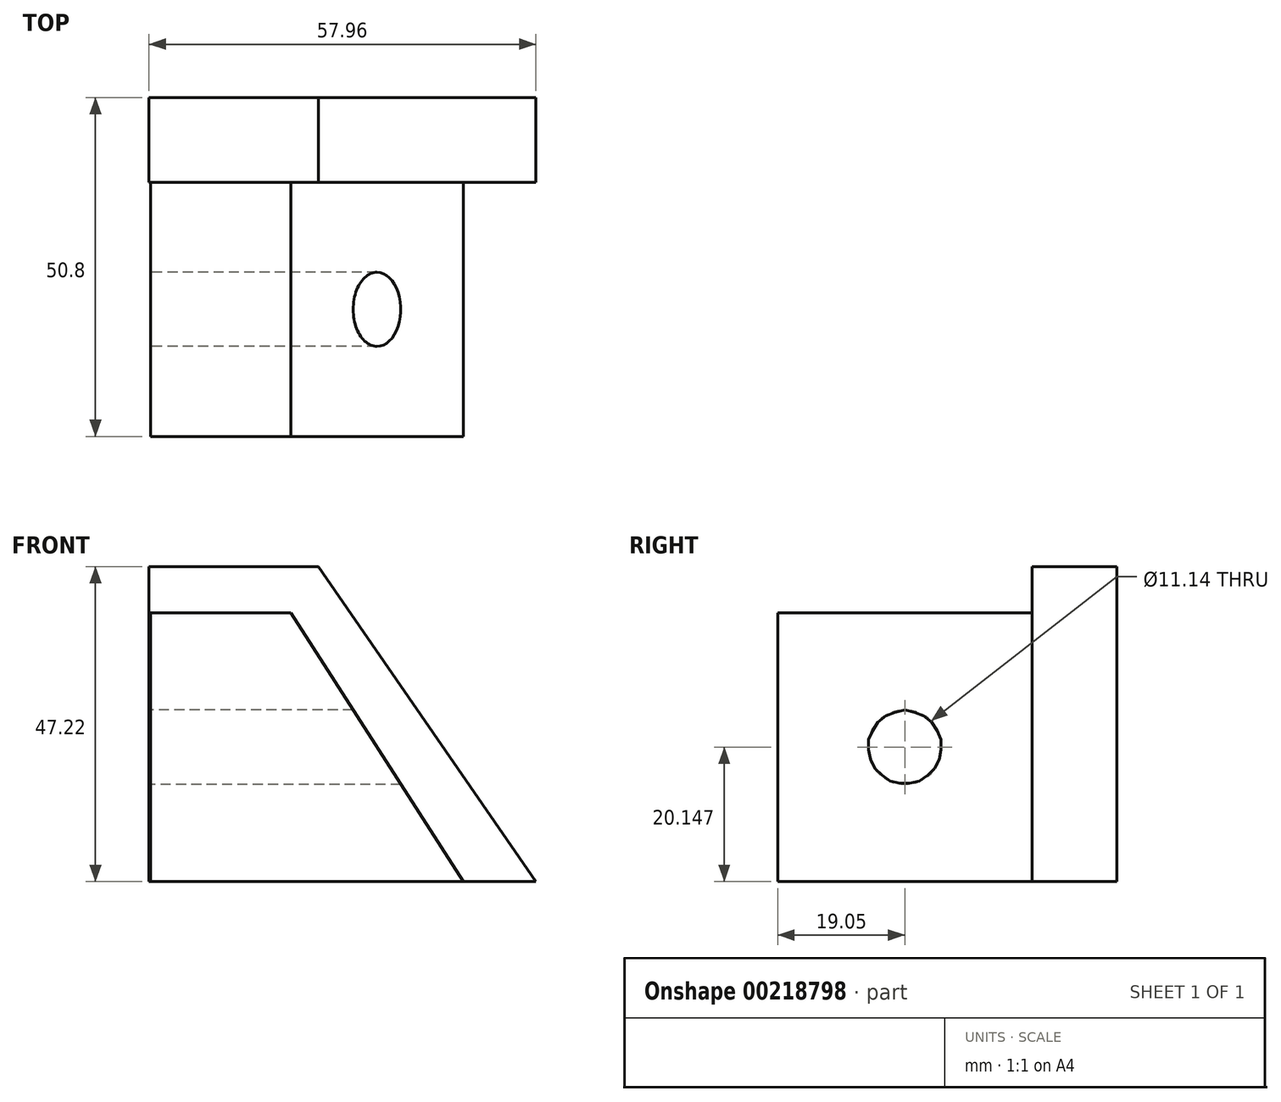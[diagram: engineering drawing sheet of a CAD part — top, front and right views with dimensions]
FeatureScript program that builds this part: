
annotation { "Feature Type Name" : "Feature", "Feature Type Description" : "" }
export const myFeature = defineFeature(function(context is Context, id is Id, definition is map)
    precondition{}
    {
        {
            var Q0;
            Q0=qCreatedBy(makeId("Front.planeOp"),FACE);
            var sketch = newSketch(context, id + "F0", { "sketchPlane" : qUnion([Q0])});
            skLineSegment(sketch, "E0", {"start": v(0, 0) * mm, "end": v(-46.87, 0) * mm});
            skLineSegment(sketch, "E1", {"start": v(-46.87, 0) * mm, "end": v(-46.87, 40.3) * mm});
            skLineSegment(sketch, "E2", {"start": v(-46.87, 40.3) * mm, "end": v(-25.86, 40.3) * mm});
            skLineSegment(sketch, "E3", {"start": v(-25.86, 40.3) * mm, "end": v(0, 0) * mm});
            skSolve(sketch);
        }
        {
            var Q0;
            Q0=makeQuery(id+"F0.imprint","IMPRINT",FACE,{"disambiguationData":[TD([[makeQuery(id+"F0.imprint","IMPRINT",EDGE,{"derivedFrom":sQuery(id+"F0.wireOp",EDGE,"E0")}),-1.0]])]});
            extrude(context, id + "F1", {"entities" : qUnion([Q0]), "depth" : 50.8 * mm});
        }
        {
            var Q0;
            Q0=qCreatedBy(makeId("Front.planeOp"),FACE);
            var sketch = newSketch(context, id + "F2", { "sketchPlane" : qUnion([Q0])});
            skLineSegment(sketch, "E4", {"start": v(-47.1, 0) * mm, "end": v(10.85, 0) * mm});
            skLineSegment(sketch, "E5", {"start": v(-47.1, 0) * mm, "end": v(-47.1, 47.22) * mm});
            skLineSegment(sketch, "E6", {"start": v(-47.1, 47.22) * mm, "end": v(-21.7, 47.22) * mm});
            skLineSegment(sketch, "E7", {"start": v(-21.7, 47.22) * mm, "end": v(10.85, 0) * mm});
            skSolve(sketch);
        }
        {
            var Q0;
            Q0=makeQuery(id+"F2.imprint","IMPRINT",FACE,{"disambiguationData":[TD([[makeQuery(id+"F2.imprint","IMPRINT",EDGE,{"derivedFrom":sQuery(id+"F2.wireOp",EDGE,"E4")}),1.0]])]});
            extrude(context, id + "F3", {"entities" : qUnion([Q0]), "operationType" : NewBodyOperationType.ADD, "depth" : 12.7 * mm});
        }
        {
            var Q0;
            Q0=makeQuery(id+"F1.opExtrude","SWEPT_FACE",FACE,{"disambiguationData":[OSD([sQuery(id+"F0.wireOp",EDGE,"E1")])]});
            var sketch = newSketch(context, id + "F4", { "sketchPlane" : qUnion([Q0])});
            skCircle(sketch, "E8", {"center": v(31.75, 20.15) * mm, "radius": 5.57 * mm});
            skPoint(sketch, "E8.centerSnap0", {"position": v(31.75, 40.3) * mm});
            skPoint(sketch, "E8.centerSnap1", {"position": v(50.8, 20.15) * mm});
            skSolve(sketch);
        }
        {
            var Q0;
            Q0 = qSketchRegion(id + "F4", true);
            extrude(context, id + "F5", {"entities" : qUnion([Q0]), "operationType" : NewBodyOperationType.REMOVE, "oppositeDirection" : true, "depth" : 50.8 * mm});
        }
    });
